# Revit family: 0041740
name_source: partatom
category: Lighting Fixtures
revit_build: Autodesk Revit 2016 (Build: 20150220_1215(x64)
units: mm (PartAtom-declared; Revit-internal decimal feet)

## family parameters
Cut with Voids When Loaded = No
Host = Face
Light Source = Yes
OmniClass Number = 23.80.70.00
OmniClass Title = Lighting
Part Type = Normal
Room Calculation Point = No
Round Connector Dimension = Use Diameter
Shared = No

## types (1)
- 0041740 SYLSAFE BAY OA C EMC NM MS
    Apparent Load = 3 VA
    Assembly Code = D5020200
    AssetType = Fixed
    ClassificationName = Uniclass2015
    ClassificationValue = EF_70_80
    Color Filter = 16777215
    Cost = 0 $
    Default Elevation = 1219 mm
    Description = SylSafe Bay OA C EMC NM MS is a dust and waterproof surface mounted emergency luminaire for industrial applications. Open area optics for standard mounting heights <4m. Non-maintained version for central battery systems. 217lm, 3W, IK03, IP65. Power Factor 0.44. Class II electrical construction.
    Dimming Lamp Color Temperature Shift = <None>
    DocumentationLiterature = http://www.sylvania-lighting.com
    ElectricShockClassification = Class II
    Emit Shape Visible in Rendering = No
    Emit from Circle Diameter = 30 mm  [stored 0.0984252 ft]
    IfcExportAs = IfcLightFixtureType
    IfcExportType = IfcLightFixtureType
    ImpactProtectionIndex = IK03
    IngressProtection = IP65
    Keynote = 16500
    Lamp = LED
    LampColourRenderingIndex = 75
    LampColourTemperature = 5700 K
    LampNominalLuminous = 217 lm
    LampsType = LED
    LuminousEfficacy = 72 lm/W
    Manufacturer = Feilo Sylvania
    ManufacturerName = Feilo Sylvania
    Material_1_SYL = PC/ABS Plastic
    Material_2_SYL = Polycarbonate, Clear
    Material_3_SYL = LED-Sylvania
    Material_4_SYL = <By Category>
    Model = SylSafe Bay OA C EMC NM MS
    ModelNumber = 0041740
    ModelReference = SylSafe Bay OA C EMC NM MS
    Name = SylSafe Bay OA C EMC NM MS
    NominalDepth = 197 mm
    NominalHeight = 53 mm  [stored 0.173885 ft]
    NominalLength = 197 mm
    Photometric Web File = 0041740.ies
    PowerConsumption = 3 W
    PowerFactor = 0.44
    Tilt Angle = -90.00°
    Type Image = <None>
    TypeName = SylSafe Bay OA C EMC NM MS
    URL = http://www.sylvania-lighting.com
    Voltage = 0 V
    Weight = 0.0 kg

note: [stored X ft] marks values corroborated as IEEE doubles in the binary element streams (Revit-internal decimal feet)

## geometry (parser evidence)
native form markers: Sweep x3
no freeform markers — native parametric forms only
